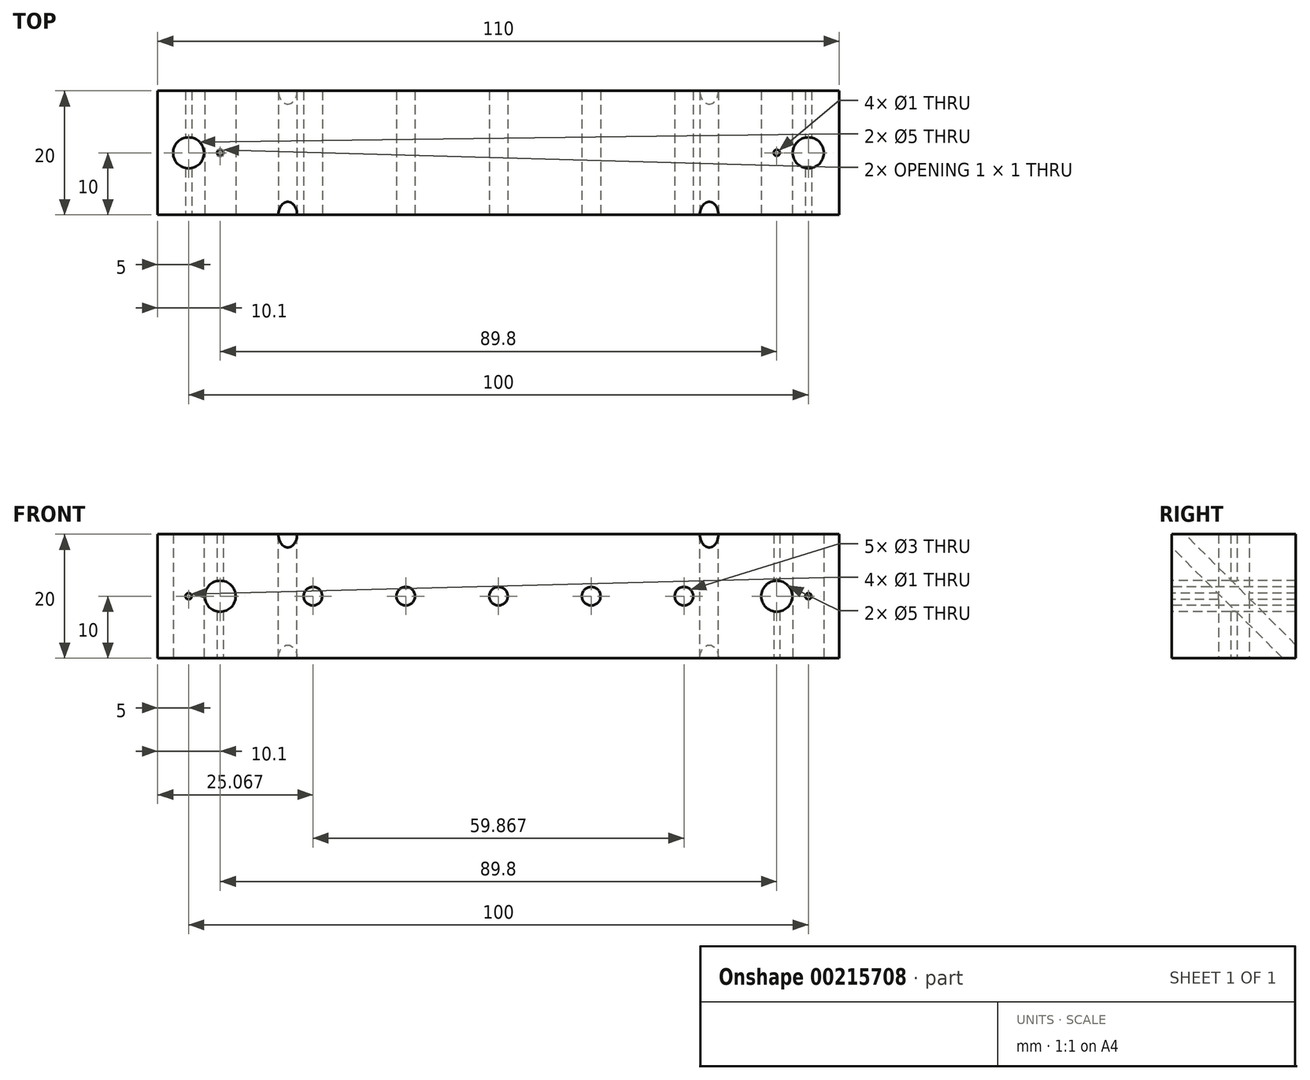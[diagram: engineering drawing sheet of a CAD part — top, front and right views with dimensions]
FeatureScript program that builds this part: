
annotation { "Feature Type Name" : "Feature", "Feature Type Description" : "" }
export const myFeature = defineFeature(function(context is Context, id is Id, definition is map)
    precondition{}
    {
        {
            var Q0;
            Q0=qCreatedBy(makeId("Top.planeOp"),FACE);
            var sketch = newSketch(context, id + "F0", { "sketchPlane" : qUnion([Q0])});
            skLineSegment(sketch, "E0.bottom", {"start": v(-55, 10) * mm, "end": v(55, 10) * mm});
            skLineSegment(sketch, "E0.top", {"start": v(-55, -10) * mm, "end": v(55, -10) * mm});
            skLineSegment(sketch, "E0.left", {"start": v(-55, 10) * mm, "end": v(-55, -10) * mm});
            skLineSegment(sketch, "E0.right", {"start": v(55, 10) * mm, "end": v(55, -10) * mm});
            skLineSegment(sketch, "E1", {"start": v(-55, 10) * mm, "end": v(55, -10) * mm, "construction": true});
            skCircle(sketch, "E2", {"center": v(-50, 0) * mm, "radius": 2.5 * mm});
            skCircle(sketch, "E3.MirrorC", {"center": v(50, 0) * mm, "radius": 2.5 * mm});
            skCircle(sketch, "E4", {"center": v(-44.9, 0) * mm, "radius": 0.5 * mm});
            skCircle(sketch, "E5.MirrorC", {"center": v(44.9, 0) * mm, "radius": 0.5 * mm});
            skSolve(sketch);
        }
        {
            var Q0;
            Q0 = qSketchRegion(id + "F0", true);
            extrude(context, id + "F1", {"entities" : qUnion([Q0]), "depth" : 20 * mm});
        }
        {
            var Q0;
            Q0=makeQuery(id+"F1.opExtrude","CAP_EDGE",EDGE,{"disambiguationData":[OSD([sQuery(id+"F0.wireOp",EDGE,"E0.top")])],"isStart":false});
            cPlane(context, id + "F2", {"entities" : qUnion([Q0]), "cplaneType" : CPlaneType.LINE_ANGLE, "offset" : 25 * mm, "angle" : 135 * degree, "width" : 150 * mm, "height" : 150 * mm});
        }
        {
            var Q0;
            Q0=qCreatedBy(id+"F2.planeOp",FACE);
            var sketch = newSketch(context, id + "F3", { "sketchPlane" : qUnion([Q0])});
            skCircle(sketch, "E6", {"center": v(-34, 7.07) * mm, "radius": 1.5 * mm});
            skCircle(sketch, "E7.MirrorC", {"center": v(34, 7.07) * mm, "radius": 1.5 * mm});
            skSolve(sketch);
        }
        {
            var Q0;
            Q0 = qSketchRegion(id + "F3", true);
            extrude(context, id + "F4", {"entities" : qUnion([Q0]), "operationType" : NewBodyOperationType.REMOVE, "endBound" : BoundingType.THROUGH_ALL, "oppositeDirection" : true, "depth" : 25 * mm});
        }
        {
            var Q0;
            Q0=makeQuery(id+"F1.opExtrude","SWEPT_FACE",FACE,{"disambiguationData":[OSD([sQuery(id+"F0.wireOp",EDGE,"E0.top")])]});
            var sketch = newSketch(context, id + "F5", { "sketchPlane" : qUnion([Q0])});
            skCircle(sketch, "E8", {"center": v(-44.9, 10) * mm, "radius": 2.5 * mm});
            skPoint(sketch, "E8.centerSnap0", {"position": v(-55, 10) * mm});
            skCircle(sketch, "E9.MirrorC", {"center": v(44.9, 10) * mm, "radius": 2.5 * mm});
            skCircle(sketch, "E10", {"center": v(-50, 10) * mm, "radius": 0.5 * mm});
            skCircle(sketch, "E11", {"center": v(-29.93, 10) * mm, "radius": 1.5 * mm});
            skCircle(sketch, "E12", {"center": v(-14.97, 10) * mm, "radius": 1.5 * mm});
            skCircle(sketch, "E13", {"center": v(0, 10) * mm, "radius": 1.5 * mm});
            skCircle(sketch, "E14", {"center": v(14.97, 10) * mm, "radius": 1.5 * mm});
            skCircle(sketch, "E15", {"center": v(29.93, 10) * mm, "radius": 1.5 * mm});
            skCircle(sketch, "E16.MirrorC", {"center": v(50, 10) * mm, "radius": 0.5 * mm});
            skSolve(sketch);
        }
        {
            var Q0;
            Q0 = qSketchRegion(id + "F5", true);
            extrude(context, id + "F6", {"entities" : qUnion([Q0]), "operationType" : NewBodyOperationType.REMOVE, "endBound" : BoundingType.THROUGH_ALL, "oppositeDirection" : true, "depth" : 25 * mm});
        }
    });
